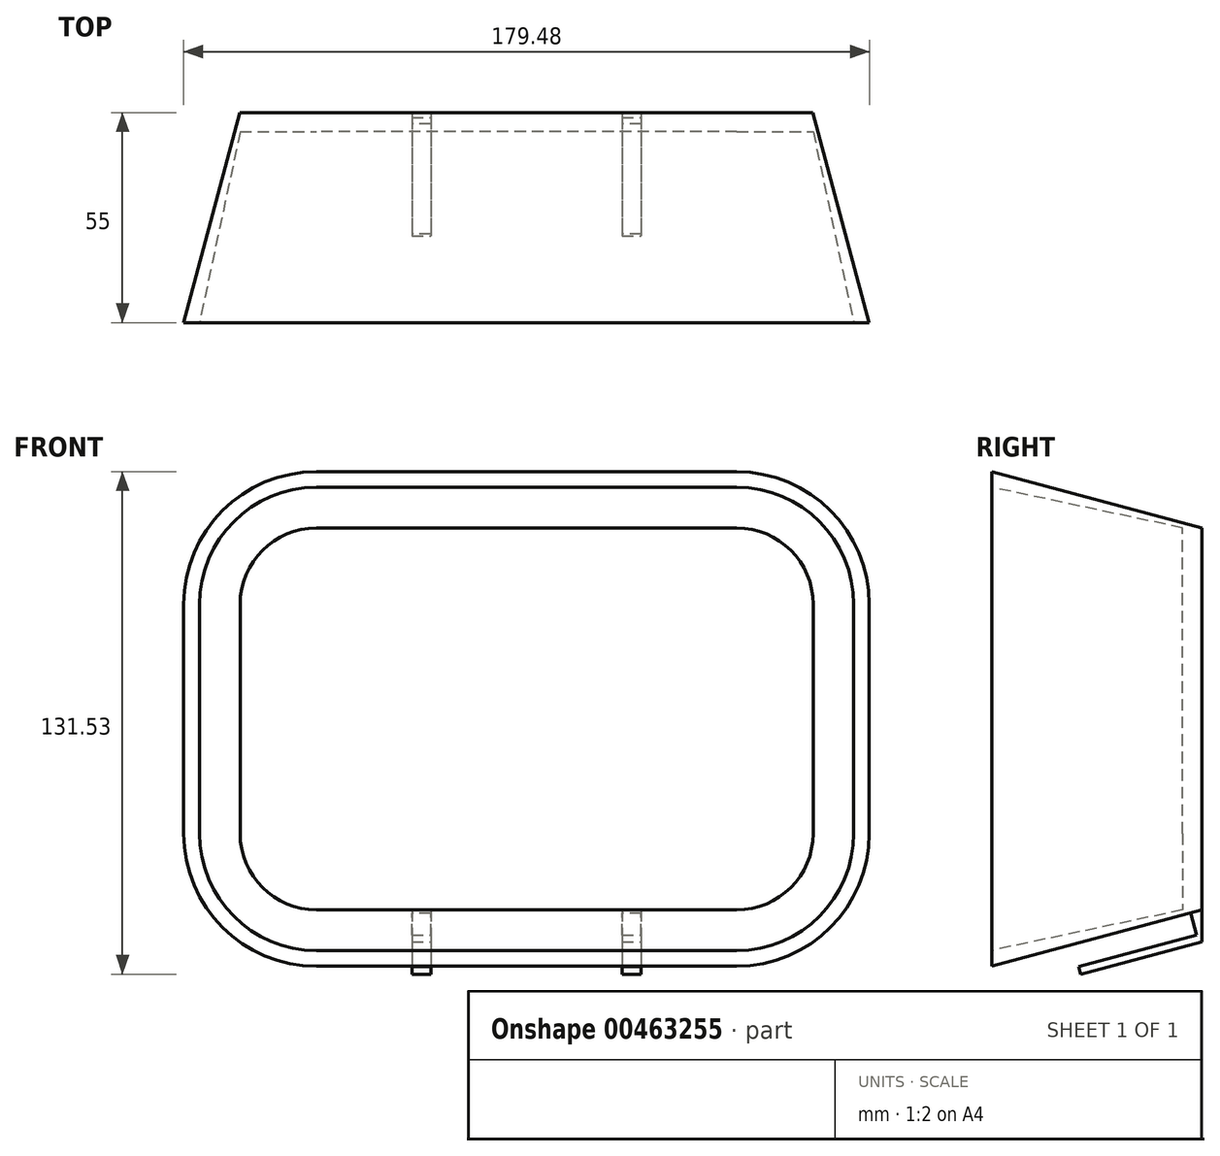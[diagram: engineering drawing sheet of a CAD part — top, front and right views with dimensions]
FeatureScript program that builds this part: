
annotation { "Feature Type Name" : "Feature", "Feature Type Description" : "" }
export const myFeature = defineFeature(function(context is Context, id is Id, definition is map)
    precondition{}
    {
        {
            var Q0;
            Q0=qCreatedBy(makeId("Front.planeOp"),FACE);
            var sketch = newSketch(context, id + "F0", { "sketchPlane" : qUnion([Q0])});
            skLineSegment(sketch, "E0.bottom", {"start": v(-105.92, 85.19) * mm, "end": v(4.08, 85.19) * mm});
            skLineSegment(sketch, "E0.top", {"start": v(-105.92, -14.81) * mm, "end": v(4.08, -14.81) * mm});
            skLineSegment(sketch, "E0.left", {"start": v(-125.92, 65.19) * mm, "end": v(-125.92, 5.19) * mm});
            skLineSegment(sketch, "E0.right", {"start": v(24.08, 65.19) * mm, "end": v(24.08, 5.19) * mm});
            skPoint(sketch, "E1.visualSharp", {"position": v(24.08, 85.19) * mm});
            skArc(sketch, "E1.filletArc", {"start": v(24.08, 65.19) * mm, "mid": v(18.22, 79.33) * mm, "end": v(4.08, 85.19) * mm});
            skArc(sketch, "E2.filletArc", {"start": v(4.08, -14.81) * mm, "mid": v(18.22, -8.95) * mm, "end": v(24.08, 5.19) * mm});
            skArc(sketch, "E3.filletArc", {"start": v(-125.92, 5.19) * mm, "mid": v(-120.06, -8.95) * mm, "end": v(-105.92, -14.81) * mm});
            skPoint(sketch, "E4.visualSharp", {"position": v(-125.92, 85.19) * mm});
            skArc(sketch, "E4.filletArc", {"start": v(-105.92, 85.19) * mm, "mid": v(-120.06, 79.33) * mm, "end": v(-125.92, 65.19) * mm});
            skSolve(sketch);
        }
        {
            var Q0;
            Q0=makeQuery(id+"F0.imprint","IMPRINT",FACE,{"disambiguationData":[TD([[makeQuery(id+"F0.imprint","IMPRINT",EDGE,{"derivedFrom":sQuery(id+"F0.wireOp",EDGE,"E0.bottom")}),-1.0]])]});
            extrude(context, id + "F1", {"entities" : qUnion([Q0]), "depth" : 55 * mm, "hasDraft" : true, "draftAngle" : 15 * degree});
        }
        {
            var Q0;
            Q0=makeQuery(id+"F1.opExtrude","CAP_FACE",FACE,{"disambiguationData":[OSD([sQuery(id+"F0.wireOp",EDGE,"E0.bottom"),sQuery(id+"F0.wireOp",EDGE,"E0.top"),sQuery(id+"F0.wireOp",EDGE,"E0.left"),sQuery(id+"F0.wireOp",EDGE,"E0.right"),sQuery(id+"F0.wireOp",EDGE,"E1.filletArc"),sQuery(id+"F0.wireOp",EDGE,"E2.filletArc"),sQuery(id+"F0.wireOp",EDGE,"E3.filletArc"),sQuery(id+"F0.wireOp",EDGE,"E4.filletArc")])],"isStart":false});
            cPlane(context, id + "F2", {"entities" : qUnion([Q0]), "cplaneType" : CPlaneType.OFFSET, "offset" : 50 * mm, "oppositeDirection" : true, "width" : 150 * mm, "height" : 150 * mm});
        }
        {
            var Q0;
            Q0=qCreatedBy(id+"F2.planeOp",FACE);
            var sketch = newSketch(context, id + "F3", { "sketchPlane" : qUnion([Q0])});
            skLineSegment(sketch, "E5.bottom", {"start": v(-105.9, 85.22) * mm, "end": v(4.1, 85.22) * mm});
            skLineSegment(sketch, "E5.top", {"start": v(-105.9, -14.78) * mm, "end": v(4.1, -14.78) * mm});
            skLineSegment(sketch, "E5.left", {"start": v(-125.9, 65.22) * mm, "end": v(-125.9, 5.22) * mm});
            skLineSegment(sketch, "E5.right", {"start": v(24.1, 65.22) * mm, "end": v(24.1, 5.22) * mm});
            skPoint(sketch, "E6.visualSharp", {"position": v(-125.9, 85.22) * mm});
            skArc(sketch, "E6.filletArc", {"start": v(-105.9, 85.22) * mm, "mid": v(-120.04, 79.36) * mm, "end": v(-125.9, 65.22) * mm});
            skPoint(sketch, "E7.visualSharp", {"position": v(-125.9, -14.78) * mm});
            skArc(sketch, "E7.filletArc", {"start": v(-125.9, 5.22) * mm, "mid": v(-120.04, -8.92) * mm, "end": v(-105.9, -14.78) * mm});
            skPoint(sketch, "E8.visualSharp", {"position": v(24.1, -14.78) * mm});
            skArc(sketch, "E8.filletArc", {"start": v(4.1, -14.78) * mm, "mid": v(18.25, -8.92) * mm, "end": v(24.1, 5.22) * mm});
            skPoint(sketch, "E9.visualSharp", {"position": v(24.1, 85.22) * mm});
            skArc(sketch, "E9.filletArc", {"start": v(24.1, 65.22) * mm, "mid": v(18.25, 79.36) * mm, "end": v(4.1, 85.22) * mm});
            skSolve(sketch);
        }
        {
            var Q0;
            Q0=qSketchRegion(id+"F3",true);
            extrude(context, id + "F4", {"entities" : qUnion([Q0]), "operationType" : NewBodyOperationType.REMOVE, "depth" : 55 * mm, "hasDraft" : true, "draftAngle" : 12 * degree});
        }
        {
            var Q0;
            Q0=makeQuery(id+"F1.opExtrude","SWEPT_FACE",FACE,{"disambiguationData":[OSD([sQuery(id+"F0.wireOp",EDGE,"E0.right")])]});
            var sketch = newSketch(context, id + "F5", { "sketchPlane" : qUnion([Q0])});
            skLineSegment(sketch, "E10.bottom", {"start": v(-62.17, 94.93) * mm, "end": v(-6.23, 94.93) * mm});
            skLineSegment(sketch, "E10.top", {"start": v(-62.17, 5.19) * mm, "end": v(-6.23, 5.19) * mm});
            skLineSegment(sketch, "E10.left", {"start": v(-62.17, 94.93) * mm, "end": v(-62.17, 5.19) * mm});
            skLineSegment(sketch, "E10.right", {"start": v(-6.23, 94.93) * mm, "end": v(-6.23, 5.19) * mm});
            skSolve(sketch);
        }
        {
            var Q0;
            Q0=qCreatedBy(makeId("Front.planeOp"),FACE);
            var sketch = newSketch(context, id + "F6", { "sketchPlane" : qUnion([Q0])});
            skLineSegment(sketch, "E11.bottom", {"start": v(185.4, 123.91) * mm, "end": v(-174.62, 123.91) * mm});
            skLineSegment(sketch, "E11.top", {"start": v(185.4, -101.96) * mm, "end": v(-174.62, -101.96) * mm});
            skLineSegment(sketch, "E11.left", {"start": v(185.4, 123.91) * mm, "end": v(185.4, -101.96) * mm});
            skLineSegment(sketch, "E11.right", {"start": v(-174.62, 123.91) * mm, "end": v(-174.62, -101.96) * mm});
            skSolve(sketch);
        }
        {
            var Q0;
            Q0=qSketchRegion(id+"F6",true);
            extrude(context, id + "F7", {"entities" : qUnion([Q0]), "operationType" : NewBodyOperationType.REMOVE, "oppositeDirection" : true, "depth" : 25 * mm});
        }
        {
            var Q0;
            Q0=makeQuery(id+"F5.imprint","IMPRINT",FACE,{"disambiguationData":[TD([[makeQuery(id+"F5.imprint","IMPRINT",EDGE,{"derivedFrom":sQuery(id+"F5.wireOp",EDGE,"E10.bottom")}),-1.0]])]});
            extrude(context, id + "F8", {"entities" : qUnion([Q0]), "operationType" : NewBodyOperationType.ADD, "depth" : 25 * mm});
        }
        {
            var Q0;
            Q0=qCreatedBy(makeId("Front.planeOp"),FACE);
            var sketch = newSketch(context, id + "F9", { "sketchPlane" : qUnion([Q0])});
            skLineSegment(sketch, "E12.bottom", {"start": v(-173.75, 128.8) * mm, "end": v(173.98, 128.8) * mm});
            skLineSegment(sketch, "E12.top", {"start": v(-173.75, -88.43) * mm, "end": v(173.98, -88.43) * mm});
            skLineSegment(sketch, "E12.left", {"start": v(-173.75, 128.8) * mm, "end": v(-173.75, -88.43) * mm});
            skLineSegment(sketch, "E12.right", {"start": v(173.98, 128.8) * mm, "end": v(173.98, -88.43) * mm});
            skSolve(sketch);
        }
        {
            var Q0;
            Q0=qSketchRegion(id+"F9",true);
            extrude(context, id + "F10", {"entities" : qUnion([Q0]), "operationType" : NewBodyOperationType.REMOVE, "oppositeDirection" : true, "depth" : 25 * mm});
        }
        {
            var Q0;
            Q0=makeQuery(id+"F1.opExtrude","SWEPT_FACE",FACE,{"disambiguationData":[OSD([sQuery(id+"F0.wireOp",EDGE,"E0.top")])]});
            var sketch = newSketch(context, id + "F11", { "sketchPlane" : qUnion([Q0])});
            skLineSegment(sketch, "E13.bottom", {"start": v(-75.92, 3.83) * mm, "end": v(-80.92, 3.83) * mm});
            skLineSegment(sketch, "E13.top", {"start": v(-75.92, 38.83) * mm, "end": v(-80.92, 38.83) * mm});
            skLineSegment(sketch, "E13.left", {"start": v(-75.92, 3.83) * mm, "end": v(-75.92, 38.83) * mm});
            skLineSegment(sketch, "E13.right", {"start": v(-80.92, 3.83) * mm, "end": v(-80.92, 38.83) * mm});
            skLineSegment(sketch, "E14.bottom", {"start": v(-20.92, 3.83) * mm, "end": v(-25.92, 3.83) * mm});
            skLineSegment(sketch, "E14.top", {"start": v(-20.92, 38.83) * mm, "end": v(-25.92, 38.83) * mm});
            skLineSegment(sketch, "E14.left", {"start": v(-20.92, 3.83) * mm, "end": v(-20.92, 38.83) * mm});
            skLineSegment(sketch, "E14.right", {"start": v(-25.92, 3.83) * mm, "end": v(-25.92, 38.83) * mm});
            skSolve(sketch);
        }
        {
            var Q0;
            Q0=makeQuery(id+"F11.imprint","IMPRINT",FACE,{"disambiguationData":[TD([[makeQuery(id+"F11.imprint","IMPRINT",EDGE,{"derivedFrom":sQuery(id+"F11.wireOp",EDGE,"E13.bottom")}),1.0]])]});
            var Q1;
            Q1=makeQuery(id+"F11.imprint","IMPRINT",FACE,{"disambiguationData":[TD([[makeQuery(id+"F11.imprint","IMPRINT",EDGE,{"derivedFrom":sQuery(id+"F11.wireOp",EDGE,"E14.bottom")}),1.0]])]});
            extrude(context, id + "F12", {"entities" : qUnion([Q0, Q1]), "operationType" : NewBodyOperationType.ADD, "depth" : 8 * mm});
        }
        {
            var Q0;
            Q0=makeQuery(id+"F10.boolean.opBoolean","MERGE",FACE,{"derivedFrom":[makeQuery(id+"F1.opExtrude","CAP_FACE",FACE,{"disambiguationData":[OSD([sQuery(id+"F0.wireOp",EDGE,"E0.bottom"),sQuery(id+"F0.wireOp",EDGE,"E0.top"),sQuery(id+"F0.wireOp",EDGE,"E0.left"),sQuery(id+"F0.wireOp",EDGE,"E0.right"),sQuery(id+"F0.wireOp",EDGE,"E1.filletArc"),sQuery(id+"F0.wireOp",EDGE,"E2.filletArc"),sQuery(id+"F0.wireOp",EDGE,"E3.filletArc"),sQuery(id+"F0.wireOp",EDGE,"E4.filletArc")])],"isStart":true}),makeQuery(id+"FbQphPuMjRcy7Zt_1.opExtrude","SWEPT_FACE",FACE,{"disambiguationData":[OSD([sQuery(id+"FumkVmrRI39znup_1.wireOp",EDGE,"gU7K7XBD-hMSE-1Chr-uc86-XtxJS9Lvrfbj.right")])]}),makeQuery(id+"F10.opExtrude","CAP_FACE",FACE,{"disambiguationData":[OSD([sQuery(id+"F9.wireOp",EDGE,"E12.bottom"),sQuery(id+"F9.wireOp",EDGE,"E12.top"),sQuery(id+"F9.wireOp",EDGE,"E12.left"),sQuery(id+"F9.wireOp",EDGE,"E12.right")])],"isStart":true})]});
            var sketch = newSketch(context, id + "F13", { "sketchPlane" : qUnion([Q0])});
            skLineSegment(sketch, "E15.bottom", {"start": v(-29.21, 2.74) * mm, "end": v(93.32, 2.74) * mm});
            skLineSegment(sketch, "E15.top", {"start": v(-29.21, -46.08) * mm, "end": v(93.32, -46.08) * mm});
            skLineSegment(sketch, "E15.left", {"start": v(-29.21, 2.74) * mm, "end": v(-29.21, -46.08) * mm});
            skLineSegment(sketch, "E15.right", {"start": v(93.32, 2.74) * mm, "end": v(93.32, -46.08) * mm});
            skSolve(sketch);
        }
        {
            var Q0;
            Q0=qSketchRegion(id+"F13",true);
            extrude(context, id + "F14", {"entities" : qUnion([Q0]), "operationType" : NewBodyOperationType.REMOVE, "depth" : 25 * mm});
        }
        {
            var Q0;
            Q0=makeQuery(id+"F12.opExtrude","SWEPT_FACE",FACE,{"disambiguationData":[OSD([sQuery(id+"F11.wireOp",EDGE,"E13.top")])]});
            var sketch = newSketch(context, id + "F15", { "sketchPlane" : qUnion([Q0])});
            skLineSegment(sketch, "E16.bottom", {"start": v(-80.92, -14.3) * mm, "end": v(-75.92, -14.3) * mm});
            skLineSegment(sketch, "E16.top", {"start": v(-80.92, -20.3) * mm, "end": v(-75.92, -20.3) * mm});
            skLineSegment(sketch, "E16.left", {"start": v(-80.92, -14.3) * mm, "end": v(-80.92, -20.3) * mm});
            skLineSegment(sketch, "E16.right", {"start": v(-75.92, -14.3) * mm, "end": v(-75.92, -20.3) * mm});
            skLineSegment(sketch, "E17.bottom", {"start": v(-11.78, -43.28) * mm, "end": v(-5.78, -43.28) * mm});
            skLineSegment(sketch, "E17.top", {"start": v(-11.78, -49.28) * mm, "end": v(-5.78, -49.28) * mm});
            skLineSegment(sketch, "E17.left", {"start": v(-11.78, -43.28) * mm, "end": v(-11.78, -49.28) * mm});
            skLineSegment(sketch, "E17.right", {"start": v(-5.78, -43.28) * mm, "end": v(-5.78, -49.28) * mm});
            skSolve(sketch);
        }
        {
            var Q0;
            Q0=qSketchRegion(id+"F15",true);
            extrude(context, id + "F16", {"entities" : qUnion([Q0]), "operationType" : NewBodyOperationType.REMOVE, "oppositeDirection" : true, "depth" : 32 * mm});
        }
        {
            var Q0;
            Q0=makeQuery(id+"F8.opExtrude","SWEPT_BODY",BODY,{"disambiguationData":[OSD([sQuery(id+"F0.wireOp",EDGE,"E0.right"),sQuery(id+"F0.wireOp",EDGE,"E1.filletArc"),sQuery(id+"F5.wireOp",EDGE,"E10.bottom"),sQuery(id+"F5.wireOp",EDGE,"E10.left"),sQuery(id+"F5.wireOp",EDGE,"E10.right")])]});
            deleteBodies(context, id + "F17", {"entities" : qUnion([Q0])});
        }
        {
            var Q0;
            Q0=makeQuery(id+"F12.opExtrude","SWEPT_FACE",FACE,{"disambiguationData":[OSD([sQuery(id+"F11.wireOp",EDGE,"E14.top")])]});
            var sketch = newSketch(context, id + "F18", { "sketchPlane" : qUnion([Q0])});
            skLineSegment(sketch, "E18.bottom", {"start": v(-25.92, -14.3) * mm, "end": v(-20.92, -14.3) * mm});
            skLineSegment(sketch, "E18.top", {"start": v(-25.92, -20.3) * mm, "end": v(-20.92, -20.3) * mm});
            skLineSegment(sketch, "E18.left", {"start": v(-25.92, -14.3) * mm, "end": v(-25.92, -20.3) * mm});
            skLineSegment(sketch, "E18.right", {"start": v(-20.92, -14.3) * mm, "end": v(-20.92, -20.3) * mm});
            skSolve(sketch);
        }
        {
            var Q0;
            Q0 = qSketchRegion(id + "F18", true);
            extrude(context, id + "F19", {"entities" : qUnion([Q0]), "operationType" : NewBodyOperationType.REMOVE, "oppositeDirection" : true, "depth" : 32 * mm});
        }
    });
